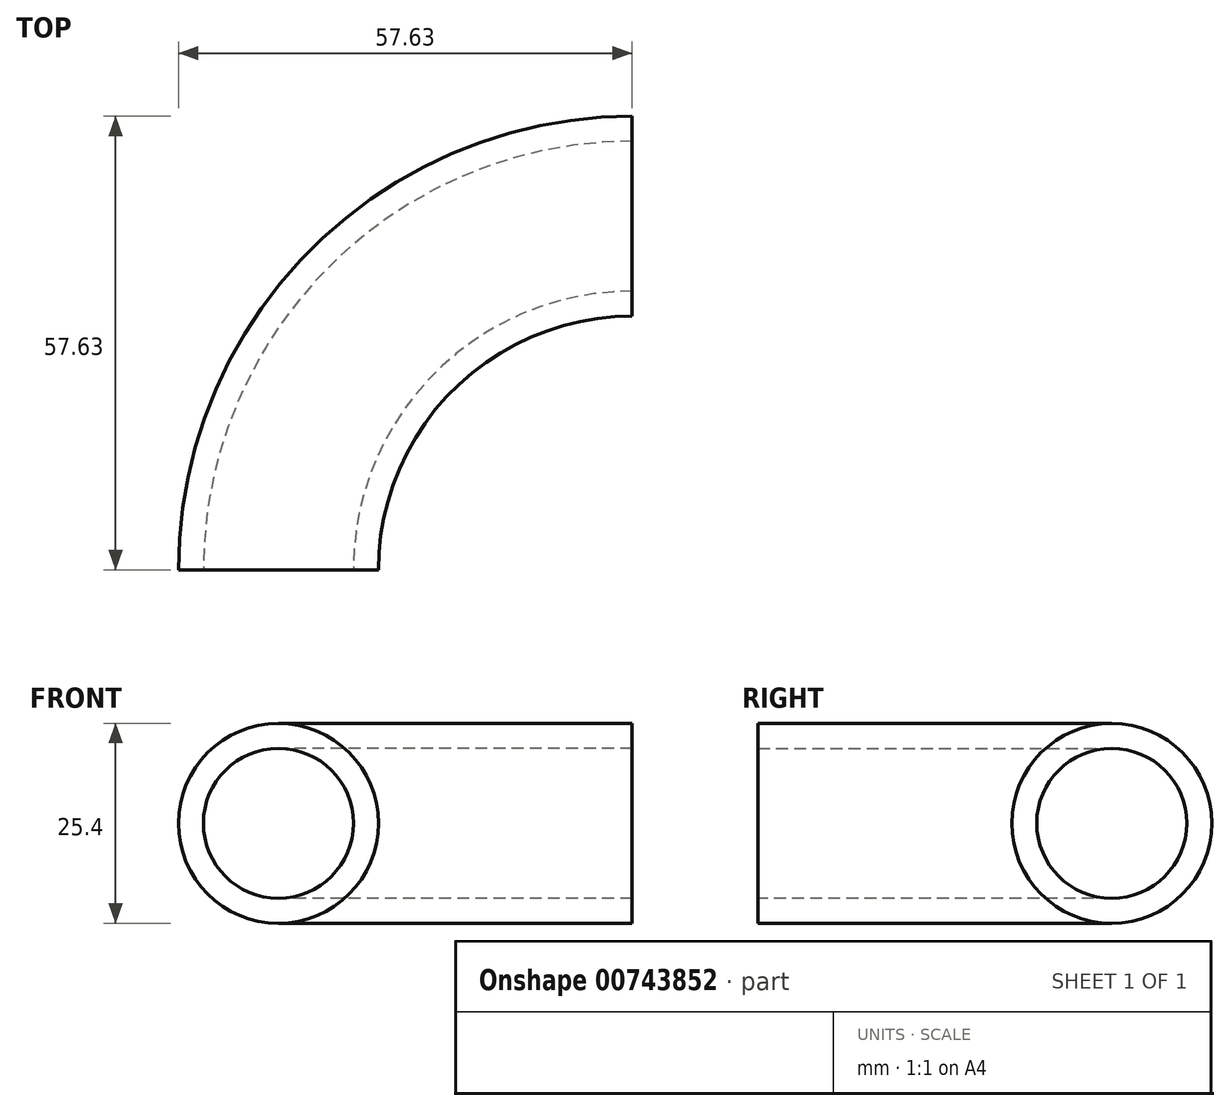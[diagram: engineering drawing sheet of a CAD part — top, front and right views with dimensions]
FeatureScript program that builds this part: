
annotation { "Feature Type Name" : "Feature", "Feature Type Description" : "" }
export const myFeature = defineFeature(function(context is Context, id is Id, definition is map)
    precondition{}
    {
        {
            var Q0;
            Q0=qCreatedBy(makeId("Front.planeOp"),FACE);
            var sketch = newSketch(context, id + "F0", { "sketchPlane" : qUnion([Q0])});
            skCircle(sketch, "E0", {"center": v(0, 0) * mm, "radius": 9.53 * mm});
            skCircle(sketch, "E1", {"center": v(0, 0) * mm, "radius": 12.7 * mm});
            skSolve(sketch);
        }
        {
            var Q0;
            Q0=qCreatedBy(makeId("Front.planeOp"),FACE);
            var sketch = newSketch(context, id + "F1", { "sketchPlane" : qUnion([Q0])});
            skLineSegment(sketch, "E2", {"start": v(44.93, 54.61) * mm, "end": v(44.93, -36.87) * mm});
            skSolve(sketch);
        }
        {
            var Q0;
            Q0=makeQuery(id+"F0.imprint","IMPRINT",FACE,{"disambiguationData":[TD([[makeQuery(id+"F0.imprint","IMPRINT",EDGE,{"derivedFrom":sQuery(id+"F0.wireOp",EDGE,"E0")}),-1.0]])]});
            var Q1;
            Q1=sQuery(id+"F1.wireOp",EDGE,"E2");
            revolve(context, id + "F2", {"surfaceOperationType" : NewSurfaceOperationType.NEW, "entities" : qUnion([Q0]), "axis" : qUnion([Q1]), "revolveType" : RevolveType.ONE_DIRECTION, "angle" : 90 * degree});
        }
    });
